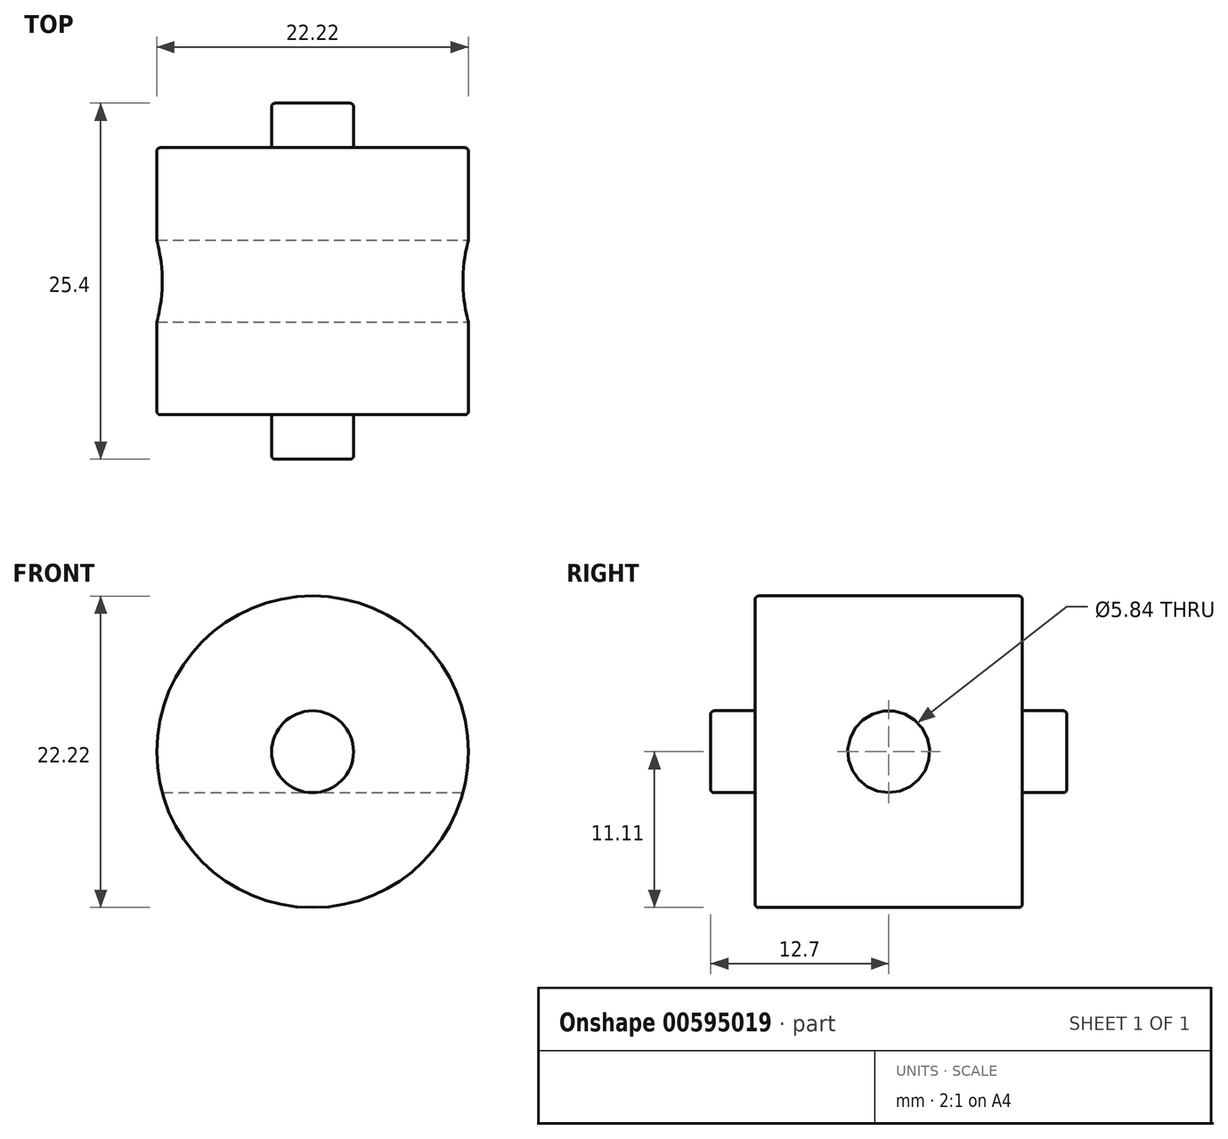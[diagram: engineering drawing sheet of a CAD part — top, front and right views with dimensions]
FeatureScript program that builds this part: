
annotation { "Feature Type Name" : "Feature", "Feature Type Description" : "" }
export const myFeature = defineFeature(function(context is Context, id is Id, definition is map)
    precondition{}
    {
        {
            var Q0;
            Q0=qCreatedBy(makeId("Front.planeOp"),FACE);
            var sketch = newSketch(context, id + "F0", { "sketchPlane" : qUnion([Q0])});
            skCircle(sketch, "E0", {"center": v(0, 0) * mm, "radius": 11.11 * mm});
            skSolve(sketch);
        }
        {
            var Q0;
            Q0=qCreatedBy(makeId("Front.planeOp"),FACE);
            var sketch = newSketch(context, id + "F1", { "sketchPlane" : qUnion([Q0])});
            skCircle(sketch, "E1", {"center": v(0, 0) * mm, "radius": 2.92 * mm});
            skSolve(sketch);
        }
        {
            var Q0;
            Q0=qCreatedBy(makeId("Right.planeOp"),FACE);
            var sketch = newSketch(context, id + "F2", { "sketchPlane" : qUnion([Q0])});
            skCircle(sketch, "E2", {"center": v(0, 0) * mm, "radius": 2.92 * mm});
            skSolve(sketch);
        }
        {
            var Q0;
            Q0 = qSketchRegion(id + "F0", true);
            extrude(context, id + "F3", {"entities" : qUnion([Q0]), "endBound" : BoundingType.SYMMETRIC, "depth" : 19.05 * mm, "offsetDistance" : 25.4 * mm});
        }
        {
            var Q0;
            Q0 = qSketchRegion(id + "F1", true);
            extrude(context, id + "F4", {"entities" : qUnion([Q0]), "operationType" : NewBodyOperationType.ADD, "endBound" : BoundingType.SYMMETRIC, "depth" : 25.4 * mm, "offsetDistance" : 25.4 * mm});
        }
        {
            var Q0;
            Q0 = qSketchRegion(id + "F2", true);
            extrude(context, id + "F5", {"entities" : qUnion([Q0]), "operationType" : NewBodyOperationType.REMOVE, "endBound" : BoundingType.SYMMETRIC, "oppositeDirection" : true, "depth" : 25.4 * mm, "offsetDistance" : 25.4 * mm});
        }
        {
            var Q0;
            Q0=makeQuery(id+"F4.opExtrude","CAP_EDGE",EDGE,{"disambiguationData":[OSD([sQuery(id+"F1.wireOp",EDGE,"E1")])],"isStart":false});
            var Q1;
            Q1=makeQuery(id+"F3.opExtrude","CAP_EDGE",EDGE,{"disambiguationData":[OSD([sQuery(id+"F0.wireOp",EDGE,"E0")])],"isStart":false});
            var Q2;
            Q2=makeQuery(id+"F3.opExtrude","CAP_EDGE",EDGE,{"disambiguationData":[OSD([sQuery(id+"F0.wireOp",EDGE,"E0")])],"isStart":true});
            var Q3;
            Q3=makeQuery(id+"F4.opExtrude","CAP_EDGE",EDGE,{"disambiguationData":[OSD([sQuery(id+"F1.wireOp",EDGE,"E1")])],"isStart":true});
            fillet(context, id + "F6", {"entities" : qUnion([Q0, Q1, Q2, Q3]), "radius" : 0.25 * mm, "allowEdgeOverflow" : false});
        }
    });
